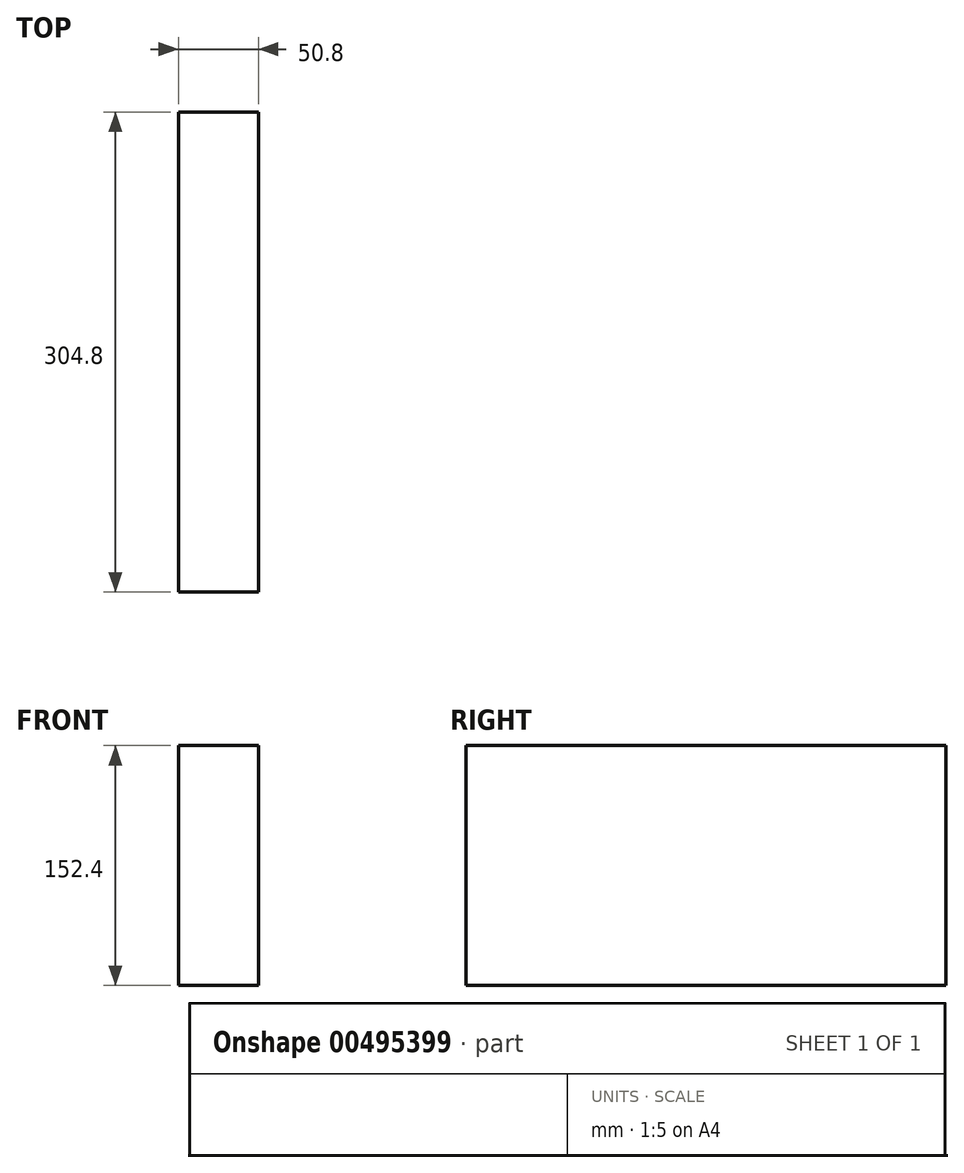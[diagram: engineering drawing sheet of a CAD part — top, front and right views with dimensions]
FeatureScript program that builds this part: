
annotation { "Feature Type Name" : "Feature", "Feature Type Description" : "" }
export const myFeature = defineFeature(function(context is Context, id is Id, definition is map)
    precondition{}
    {
        {
            var Q0;
            Q0=qCreatedBy(makeId("Front.planeOp"),FACE);
            var sketch = newSketch(context, id + "F0", { "sketchPlane" : qUnion([Q0])});
            skLineSegment(sketch, "E0.bottom", {"start": v(0, 0) * mm, "end": v(50.8, 0) * mm});
            skLineSegment(sketch, "E0.top", {"start": v(0, 152.4) * mm, "end": v(50.8, 152.4) * mm});
            skLineSegment(sketch, "E0.left", {"start": v(0, 0) * mm, "end": v(0, 152.4) * mm});
            skLineSegment(sketch, "E0.right", {"start": v(50.8, 0) * mm, "end": v(50.8, 152.4) * mm});
            skSolve(sketch);
        }
        {
            var Q0;
            Q0 = qSketchRegion(id + "F0", true);
            extrude(context, id + "F1", {"entities" : qUnion([Q0]), "depth" : 304.8 * mm, "offsetDistance" : 25.4 * mm});
        }
    });
